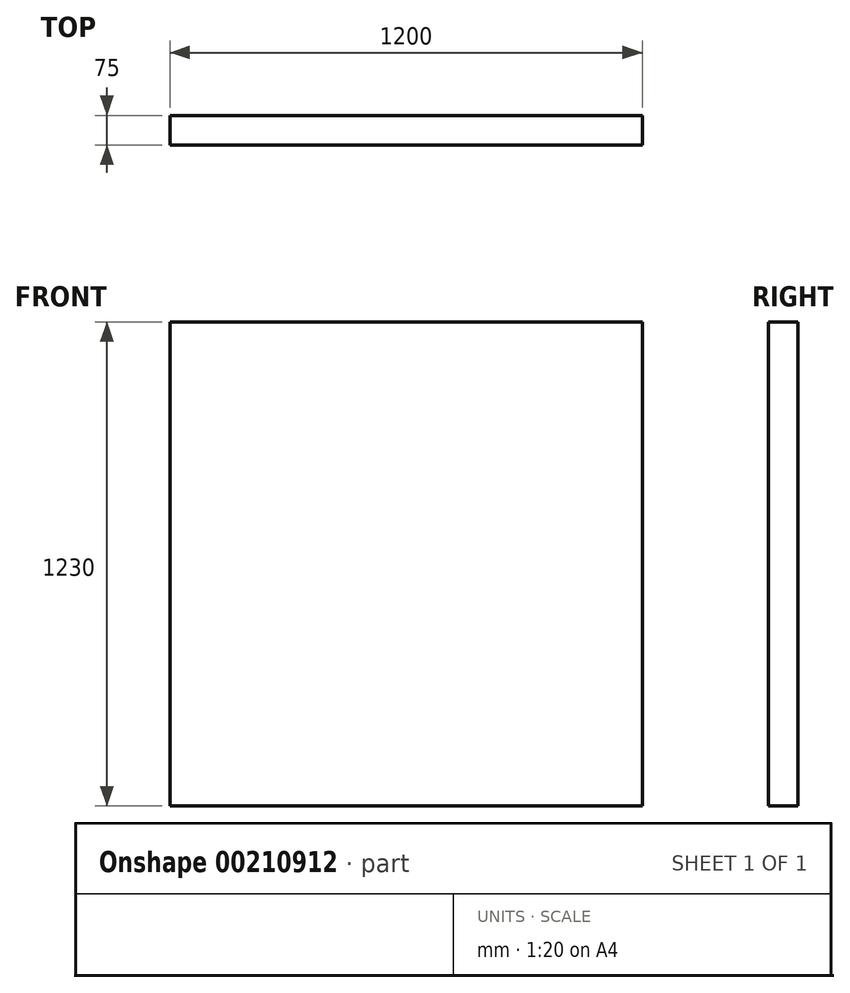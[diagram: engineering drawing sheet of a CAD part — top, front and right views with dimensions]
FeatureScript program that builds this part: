
annotation { "Feature Type Name" : "Feature", "Feature Type Description" : "" }
export const myFeature = defineFeature(function(context is Context, id is Id, definition is map)
    precondition{}
    {
        {
            var Q0;
            Q0=qCreatedBy(makeId("Front.planeOp"),FACE);
            var sketch = newSketch(context, id + "F0", { "sketchPlane" : qUnion([Q0])});
            skLineSegment(sketch, "E0.bottom", {"start": v(0, 0) * mm, "end": v(1200, 0) * mm});
            skLineSegment(sketch, "E0.right", {"start": v(1200, 0) * mm, "end": v(1200, 1230) * mm});
            skLineSegment(sketch, "E1", {"start": v(0, 1230) * mm, "end": v(1200, 1230) * mm});
            skLineSegment(sketch, "E2", {"start": v(0, 0) * mm, "end": v(0, 1230) * mm});
            skSolve(sketch);
        }
        {
            var Q0;
            Q0=makeQuery(id+"F0.imprint","IMPRINT",FACE,{"disambiguationData":[TD([[makeQuery(id+"F0.imprint","IMPRINT",EDGE,{"derivedFrom":sQuery(id+"F0.wireOp",EDGE,"E0.bottom")}),1.0]])]});
            extrude(context, id + "F1", {"entities" : qUnion([Q0]), "depth" : 75 * mm});
        }
    });
